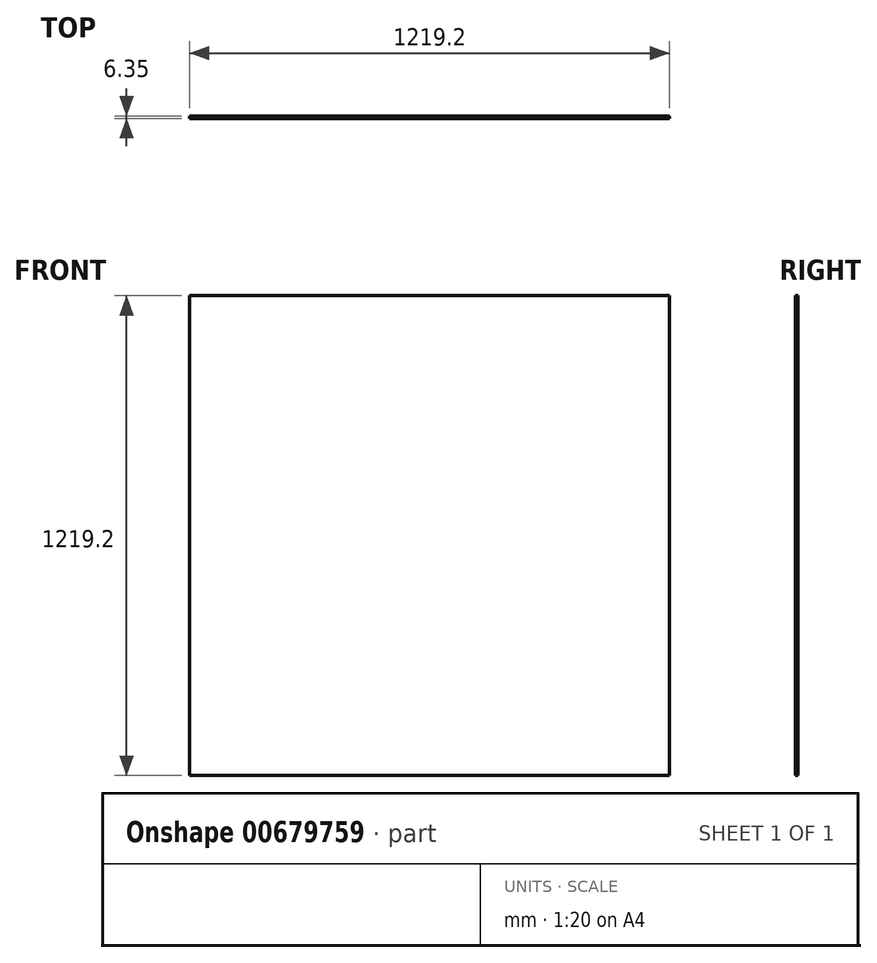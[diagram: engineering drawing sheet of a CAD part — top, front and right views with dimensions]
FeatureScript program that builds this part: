
annotation { "Feature Type Name" : "Feature", "Feature Type Description" : "" }
export const myFeature = defineFeature(function(context is Context, id is Id, definition is map)
    precondition{}
    {
        {
            var Q0;
            Q0=qCreatedBy(makeId("Front.planeOp"),FACE);
            var sketch = newSketch(context, id + "F0", { "sketchPlane" : qUnion([Q0])});
            skLineSegment(sketch, "E0.bottom", {"start": v(609.6, -609.6) * mm, "end": v(-609.6, -609.6) * mm});
            skLineSegment(sketch, "E0.top", {"start": v(609.6, 609.6) * mm, "end": v(-609.6, 609.6) * mm});
            skLineSegment(sketch, "E0.left", {"start": v(609.6, -609.6) * mm, "end": v(609.6, 609.6) * mm});
            skLineSegment(sketch, "E0.right", {"start": v(-609.6, -609.6) * mm, "end": v(-609.6, 609.6) * mm});
            skPoint(sketch, "E0.middle", {"position": v(0, 0) * mm});
            skSolve(sketch);
        }
        {
            var Q0;
            Q0 = qSketchRegion(id + "F0", true);
            extrude(context, id + "F1", {"entities" : qUnion([Q0]), "depth" : 6.35 * mm, "offsetDistance" : 30.48 * mm});
        }
    });
